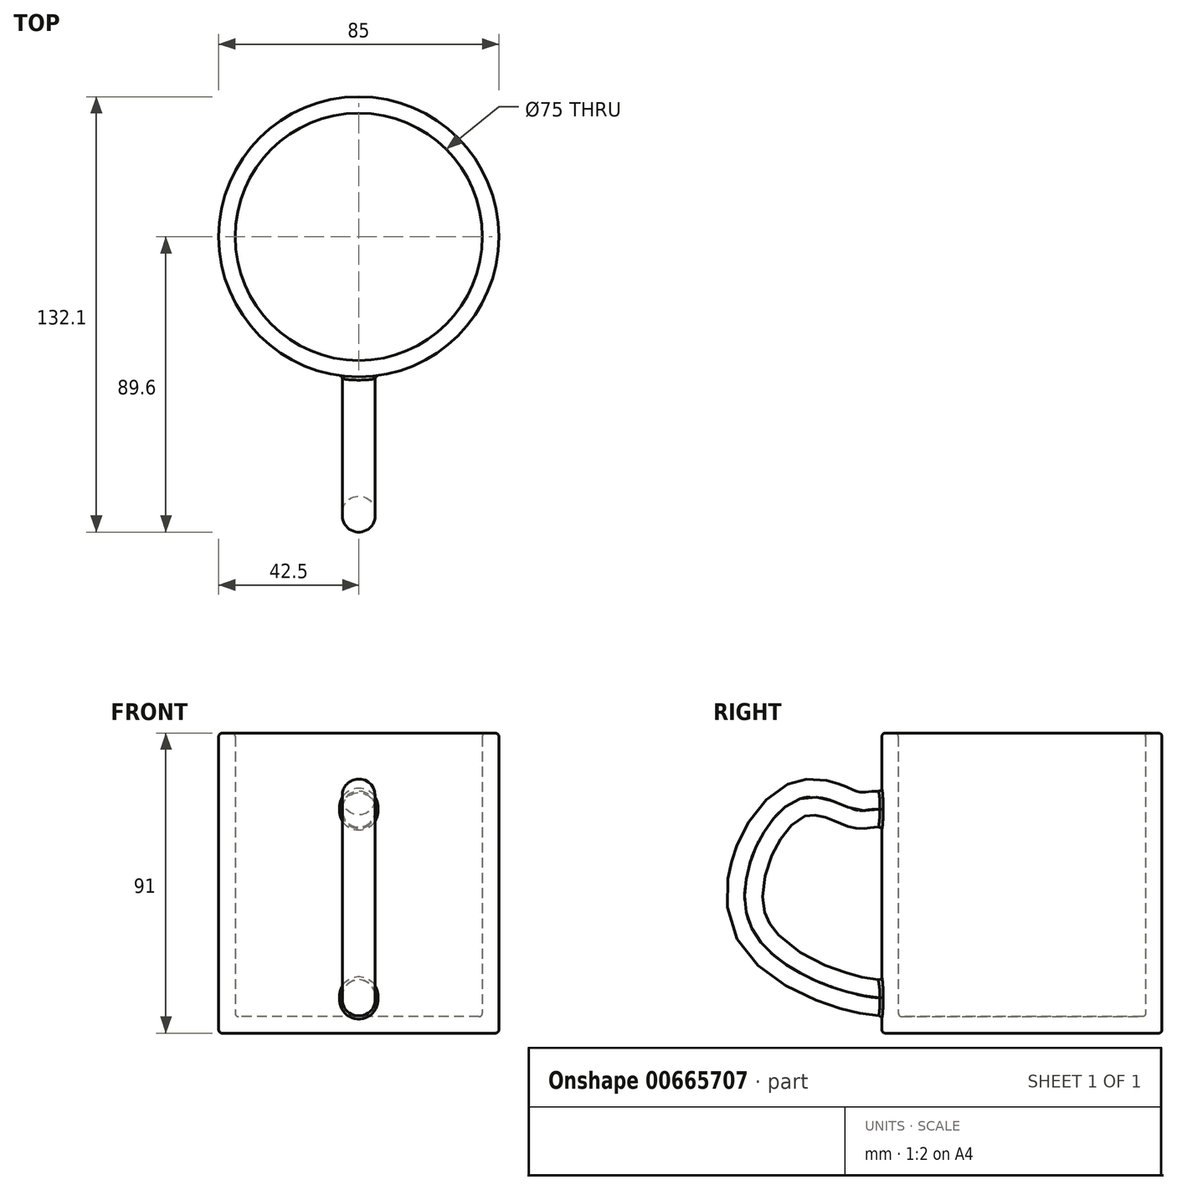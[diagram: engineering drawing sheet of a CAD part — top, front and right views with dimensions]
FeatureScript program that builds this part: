
annotation { "Feature Type Name" : "Feature", "Feature Type Description" : "" }
export const myFeature = defineFeature(function(context is Context, id is Id, definition is map)
    precondition{}
    {
        {
            var Q0;
            Q0=qCreatedBy(makeId("Top.planeOp"),FACE);
            var sketch = newSketch(context, id + "F0", { "sketchPlane" : qUnion([Q0])});
            skCircle(sketch, "E0", {"center": v(0, 0) * mm, "radius": 42.5 * mm});
            skSolve(sketch);
        }
        {
            var Q0;
            Q0 = qSketchRegion(id + "F0", true);
            extrude(context, id + "F1", {"entities" : qUnion([Q0]), "depth" : 91 * mm, "offsetDistance" : 25 * mm});
        }
        {
            var Q0;
            Q0=qCreatedBy(makeId("Front.planeOp"),FACE);
            cPlane(context, id + "F2", {"entities" : qUnion([Q0]), "cplaneType" : CPlaneType.OFFSET, "offset" : 40 * mm, "width" : 150 * mm, "height" : 150 * mm});
        }
        {
            var Q0;
            Q0=qCreatedBy(makeId("Right.planeOp"),FACE);
            var sketch = newSketch(context, id + "F3", { "sketchPlane" : qUnion([Q0])});
            skFitSpline(sketch, "E1", {"points": [v(-39.2, 68.84) * mm, v(-46.28, 68.63) * mm, v(-50.44, 68.63) * mm, v(-68.12, 71.75) * mm, v(-83.72, 33.69) * mm, v(-47.73, 10.4) * mm, v(-37.54, 10.18) * mm], "startDerivative": vector(-73.87, 0.37) * mm, "endDerivative": vector(60.81, 8.45) * mm});
            skSolve(sketch);
        }
        {
            var Q0;
            Q0=qCreatedBy(id+"F2.planeOp",FACE);
            var sketch = newSketch(context, id + "F4", { "sketchPlane" : qUnion([Q0])});
            skCircle(sketch, "E2", {"center": v(0, 68.44) * mm, "radius": 5 * mm});
            skCircle(sketch, "E3", {"center": v(0, 11.23) * mm, "radius": 5 * mm});
            skSolve(sketch);
        }
        {
            var Q0;
            Q0 = qSketchRegion(id + "F4", true);
            var Q1;
            Q1=sQuery(id+"F3.wireOp",EDGE,"E1");
            sweep(context, id + "F5", {"operationType" : NewBodyOperationType.ADD, "profiles" : qUnion([Q0]), "path" : qUnion([Q1])});
        }
        {
            var Q0;
            Q0=makeQuery(id+"F1.opExtrude","CAP_FACE",FACE,{"disambiguationData":[OSD([sQuery(id+"F0.wireOp",EDGE,"E0")])],"isStart":false});
            shell(context, id + "F6", {"entities" : qUnion([Q0]), "thickness" : 5 * mm});
        }
        {
            var Q0;
            Q0=makeQuery(id+"F1.opExtrude","CAP_EDGE",EDGE,{"disambiguationData":[OSD([sQuery(id+"F0.wireOp",EDGE,"E0")])],"isStart":false});
            var Q1;
            {var subQ0=sQuery(id+"F0.wireOp",EDGE,"E0");Q1=makeQuery(id+"F6.opShell","OFFSET_EDGE",EDGE,{"disambiguationData":[OSD([subQ0]),TDD([makeQuery(id+"F1.opExtrude","CAP_EDGE",EDGE,{"disambiguationData":[OSD([subQ0])],"isStart":false})])]});}
            var Q2;
            Q2=makeQuery(id+"F1.opExtrude","CAP_EDGE",EDGE,{"disambiguationData":[OSD([sQuery(id+"F0.wireOp",EDGE,"E0")])],"isStart":true});
            var Q3;
            Q3=makeQuery(id+"F5.boolean.opBoolean","INTERSECT",EDGE,{"disambiguationData":[OD(1.0)],"derivedFrom":[makeQuery(id+"F1.opExtrude","SWEPT_FACE",FACE,{"disambiguationData":[OSD([sQuery(id+"F0.wireOp",EDGE,"E0")])]}),makeQuery(id+"F5.opSweep","SWEPT_FACE",FACE,{"disambiguationData":[OSD([sQuery(id+"F3.wireOp",EDGE,"E1"),sQuery(id+"F4.wireOp",EDGE,"E2")])]})]});
            var Q4;
            Q4=makeQuery(id+"F5.boolean.opBoolean","INTERSECT",EDGE,{"disambiguationData":[OD(0.0)],"derivedFrom":[makeQuery(id+"F1.opExtrude","SWEPT_FACE",FACE,{"disambiguationData":[OSD([sQuery(id+"F0.wireOp",EDGE,"E0")])]}),makeQuery(id+"F5.opSweep","SWEPT_FACE",FACE,{"disambiguationData":[OSD([sQuery(id+"F3.wireOp",EDGE,"E1"),sQuery(id+"F4.wireOp",EDGE,"E2")])]})]});
            var Q5;
            Q5=makeQuery(id+"F5.boolean.opBoolean","INTERSECT",EDGE,{"disambiguationData":[OD(0.0)],"derivedFrom":[makeQuery(id+"F1.opExtrude","SWEPT_FACE",FACE,{"disambiguationData":[OSD([sQuery(id+"F0.wireOp",EDGE,"E0")])]}),makeQuery(id+"F5.opSweep","SWEPT_FACE",FACE,{"disambiguationData":[OSD([sQuery(id+"F3.wireOp",EDGE,"E1"),sQuery(id+"F4.wireOp",EDGE,"E3")])]})]});
            var Q6;
            Q6=makeQuery(id+"F5.boolean.opBoolean","INTERSECT",EDGE,{"disambiguationData":[OD(1.0)],"derivedFrom":[makeQuery(id+"F1.opExtrude","SWEPT_FACE",FACE,{"disambiguationData":[OSD([sQuery(id+"F0.wireOp",EDGE,"E0")])]}),makeQuery(id+"F5.opSweep","SWEPT_FACE",FACE,{"disambiguationData":[OSD([sQuery(id+"F3.wireOp",EDGE,"E1"),sQuery(id+"F4.wireOp",EDGE,"E3")])]})]});
            var Q7;
            {var subQ0=sQuery(id+"F0.wireOp",EDGE,"E0");Q7=makeQuery(id+"F6.opShell","OFFSET_EDGE",EDGE,{"disambiguationData":[OSD([subQ0]),TDD([makeQuery(id+"F1.opExtrude","CAP_EDGE",EDGE,{"disambiguationData":[OSD([subQ0])],"isStart":true})])]});}
            fillet(context, id + "F7", {"entities" : qUnion([Q0, Q1, Q2, Q3, Q4, Q5, Q6, Q7]), "radius" : 1 * mm, "tangentPropagation" : true, "allowEdgeOverflow" : false});
        }
    });
